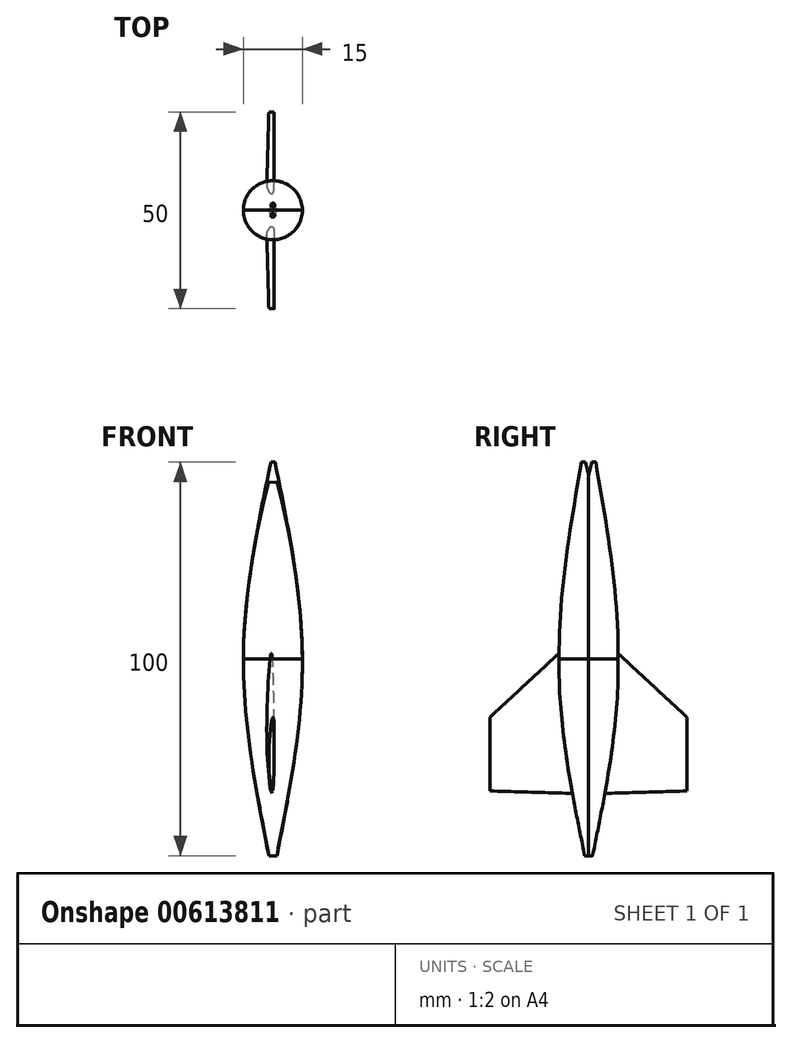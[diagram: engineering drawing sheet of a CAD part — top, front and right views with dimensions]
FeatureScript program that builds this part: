
annotation { "Feature Type Name" : "Feature", "Feature Type Description" : "" }
export const myFeature = defineFeature(function(context is Context, id is Id, definition is map)
    precondition{}
    {
        {
            var Q0;
            Q0=qCreatedBy(makeId("Top.planeOp"),FACE);
            var sketch = newSketch(context, id + "F0", { "sketchPlane" : qUnion([Q0])});
            skCircle(sketch, "E0", {"center": v(0, 0) * mm, "radius": 1 * mm});
            skSolve(sketch);
        }
        {
            var Q0;
            Q0=qCreatedBy(makeId("Top.planeOp"),FACE);
            cPlane(context, id + "F1", {"entities" : qUnion([Q0]), "cplaneType" : CPlaneType.OFFSET, "offset" : 50 * mm, "width" : 150 * mm, "height" : 150 * mm});
        }
        {
            var Q0;
            Q0=qCreatedBy(makeId("Top.planeOp"),FACE);
            cPlane(context, id + "F2", {"entities" : qUnion([Q0]), "cplaneType" : CPlaneType.OFFSET, "offset" : 100 * mm, "width" : 150 * mm, "height" : 150 * mm});
        }
        {
            var Q0;
            Q0=qCreatedBy(id+"F1.planeOp",FACE);
            var sketch = newSketch(context, id + "F3", { "sketchPlane" : qUnion([Q0])});
            skCircle(sketch, "E1", {"center": v(0, 0) * mm, "radius": 7.5 * mm});
            skSolve(sketch);
        }
        {
            var Q0;
            Q0=qCreatedBy(id+"F2.planeOp",FACE);
            var sketch = newSketch(context, id + "F4", { "sketchPlane" : qUnion([Q0])});
            skCircle(sketch, "E2", {"center": v(0, -1.3) * mm, "radius": 0.5 * mm});
            skSolve(sketch);
        }
        {
            var Q0;
            Q0 = qSketchRegion(id + "F0", true);
            var Q1;
            Q1 = qSketchRegion(id + "F3", true);
            var Q2;
            Q2 = qSketchRegion(id + "F4", true);
            loft(context, id + "F5", {"sheetProfilesArray" : [{ "sheetProfileEntities" : qUnion([Q0]) }, { "sheetProfileEntities" : qUnion([Q1]) }, { "sheetProfileEntities" : qUnion([Q2]) }]});
        }
        {
            var Q0;
            Q0=qCreatedBy(makeId("Front.planeOp"),FACE);
            cPlane(context, id + "F6", {"entities" : qUnion([Q0]), "cplaneType" : CPlaneType.OFFSET, "offset" : 25 * mm, "oppositeDirection" : true, "width" : 150 * mm, "height" : 150 * mm});
        }
        {
            var Q0;
            Q0=qCreatedBy(id+"F6.planeOp",FACE);
            var sketch = newSketch(context, id + "F7", { "sketchPlane" : qUnion([Q0])});
            skFitSpline(sketch, "E3", {"points": [v(-0.17, 16.46) * mm, v(-1.03, 23.85) * mm, v(0, 35.2) * mm, v(0.35, 26.33) * mm, v(-0.17, 16.46) * mm]});
            skSolve(sketch);
        }
        {
            var Q0;
            Q0=qCreatedBy(makeId("Front.planeOp"),FACE);
            var sketch = newSketch(context, id + "F8", { "sketchPlane" : qUnion([Q0])});
            skFitSpline(sketch, "E4", {"points": [v(-0.22, 15.73) * mm, v(-1.69, 31.17) * mm, v(-0.58, 58.37) * mm, v(0.33, 37.23) * mm, v(-0.22, 15.73) * mm]});
            skSolve(sketch);
        }
        {
            var Q1;
            Q1 = qSketchRegion(id + "F8", true);
            var Q2;
            Q2 = qSketchRegion(id + "F7", true);
            loft(context, id + "F9", {"operationType" : NewBodyOperationType.ADD, "sheetProfilesArray" : [{ "sheetProfileEntities" : qUnion([Q1]) }, { "sheetProfileEntities" : qUnion([Q2]) }]});
        }
        {
            var Q0;
            Q0=makeQuery(id+"F5.opLoft","SWEPT_BODY",BODY,{"disambiguationData":[OSD([makeQuery(id+"F0.imprint","IMPRINT",FACE,{"disambiguationData":[TD([[makeQuery(id+"F0.imprint","IMPRINT",EDGE,{"derivedFrom":sQuery(id+"F0.wireOp",EDGE,"E0")}),1.0]])]}),sQuery(id+"F3.wireOp",EDGE,"E1"),makeQuery(id+"F4.imprint","IMPRINT",FACE,{"disambiguationData":[TD([[makeQuery(id+"F4.imprint","IMPRINT",EDGE,{"derivedFrom":sQuery(id+"F4.wireOp",EDGE,"E2")}),1.0]])]})])]});
            var Q1;
            Q1=qCreatedBy(makeId("Front.planeOp"),FACE);
            mirror(context, id + "F10", {"operationType" : NewBodyOperationType.ADD, "entities" : qUnion([Q0]), "mirrorPlane" : qUnion([Q1])});
        }
    });
